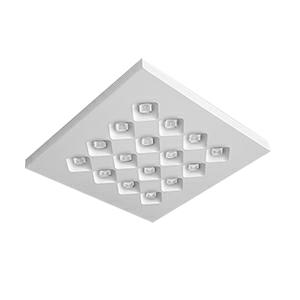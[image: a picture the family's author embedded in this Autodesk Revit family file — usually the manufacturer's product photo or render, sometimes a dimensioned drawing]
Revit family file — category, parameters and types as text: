
# Revit family: 3f_filippi_-_3f_diagon_soft_ugr_3f_filippi_-_23836_a0686_-_3f_diagon_39w-940_dali_soft_ugr_596x596___corn_plaf__04e8
name_source: partatom
category: Lighting Fixtures
units: mm (PartAtom-declared; Revit-internal decimal feet)

## family parameters
Cut with Voids When Loaded = No
Host = Face
Light Source = No
Part Type = Normal
Room Calculation Point = No
Round Connector Dimension = Use Diameter
Shared = No

## types (1)
- 3F Filippi - 3F Dìagon Soft UGR (1 x LED, 3890 lm, 40 W, 4000 K)
    Apparent Load = 40 VA
    Approval mark = CE
    CIE Flux Codes = 59 92 100 100 100
    Color Rendering = 90
    Color Temperature = 4000 K
    Control Gear = Electronic transformer
    Default Elevation = 1800 mm
    Description = ILLUMINOTECHNICAL
Luminous efficiency 100% (DLOR 100%, ULOR 0%).
Initial luminous flux of the luminaire 3890 lm.
Direct symmetric distribution.
Installation Interdistance Transv.D = 1.23 x hu - Long.D = 1.23 x hu.
Average luminance <3000 cd/m² for radial angles >65°.
Tabular UGR (CIE 117 - 4H-8H; S=0.25H; 70/50/20): RUG 18.9 - 18.9.
Beam angle: 102° - 101°.
Luminous efficacy 97 lm/W.
Lifetime (L90/B10): 30000 h. (tq+25°C)
Lifetime (L85/B10): 50000 h. (tq+25°C)
Lifetime (L80/B20): 80000 h. (tq+25°C)
Lifetime (L70/B20): 100000 h. (tq+25°C)
Sudden decreased luminous flux after 50000 hours: 0% (C0).
Photobiological safety in compliance with IEC/TR 62778: RG0 risk exempt, (IEC 62471).
In compliance with IEC/EN 62722-2-1 - IEC/EN 62717 standards.

SOURCE
Squared LED module 39W/940.
Energy efficiency class (UE 2019/2020 - UE 2019/2015): D.
CIE 13.3 Colour rendering index: CRI >90 (R9 >50%).
IES TM-30 Fidelity Index: Rf = 92 Rg = 101.
CCT nominal colour temperature 4000 K.
Colour initial tolerance (MacAdam): SDCM 3.

MECHANICAL
Housing in hot-galvanised steel, painted in white polyester.
Honeycombed diagonal screen in white anti-glare polycarbonate.
Opal methacrylate (PMMA) rhomboid lenses with differentiated, engraved and prismatic surfaces for diffused, soft lighting and excellent visual comfort.
Luminaire with limited surface temperature. - D - (EN 60598-2-24)
Dimensions: 600x600 mm, height 40 mm. Weight 6.15 kg.
IP43 protection degree for exposed part, IP20 for recessed part.
Mechanical strength to impacts IK06 (1 joule).
Glow-wire test resistance 650°C.

ELECTRICAL
Halogen Free DALI-2, PUSH-DIM, electronic wiring 230V-50/60Hz, power factor 0.97 at full load, THD <25%, constant output current, class I, 1 driver, 1 DALI addresse.
Power of the luminaire 40 W.
ENEC - CE.
SAFE FLICKER: PstLM=<1 and SVM=<0.4 (IEC TR 61547-1 and IEC TR 63158), to ensure a more comfortable and safe light.
Luminaire compliant with EN 60598-2-22 for power supply from a centralised emergency system CPSS (Central Power Supply System), not incorporated in the luminaire - high risk areas excluded. The default power and flux are 100% in AC and 15% in DC.
Ambient temperature from 0°C to +25°C.
Temperature class T6 max 85°C.
Quick connection.
Relative humidity UR: <85%.

INSTALLATION
Ceiling.
Height only 40 mm.
All accessories dedicated to this product are available on the Catalog and on our website www.3F-Filippi.com.

ACCESSORIES
A0686 - 596x596 Diagon frame for Ceiling installation.

APPLICATIONS
Environments: staterooms, with VDTs, offices.
Environments with exacting visual tasks, where diffused soft light for optimum visual comfort is required.

LIGHT MANAGEMENT
Recommended minimum setting: 10%.
The device, equipped with DALI-2 driver, can be controlled manually with 3F Easy Dim technology or automatically/manually with 3F Smart Dimming technology and/or centralised DALI systems.
DALI-2 certification guarantees interoperability with other devices with the same certification.
In electrical systems without a regulation system (manual or automatic) and DALI bus, a suitable jumper must be made on the DA-DA terminals of the appliance.

WARNING
Luminaire designed for disposal/recycling at end-of-life.
Replaceable (LED only) light source by a professional. Replaceable control gear by a professional.
    Height = 0 mm  [stored 0 ft]
    Lamp = 1 x LED
    Lamp Light Flux = 3890 lm
    Lamp Power = 40 W
    Lamp count = 1
    Length = 600 mm
    Lifetime = 50000 h
    Luminous efficacy = 97 lm/W
    Manufacturer = 3F Filippi
    ModVariant = No
    Model = 3F Filippi - 23836+A0686 - 3F Diagon 39W-940 DALI SOFT UGR 596x596 + Corn.plaf.
    Mounting Place = Ceiling
    Mounting Type = Recessed
    Number of Poles = 1
    OnlyDefault = Yes
    Power Factor = 1
    Product Name = 3F Filippi - 3F Dìagon Soft UGR
    Product group = recessed luminaire
    ProductGroupID = 4
    Protection Class = Protection class I
    Protection Degree = IP 20
    RLX_Detail_Level = 1
    RLX_Emergency_Light_Flux = 0 lm
    RLX_Emergency_Type = 0
    RLX_Emergency_Type_DB = No
    RlxData = <blob elided: 97729 chars, md5=86dff409>
    Socket = socket
    Standby Power = 0 W
    System Light Flux = 3890 lm
    System Power = 40 W
    Type Comments = Product without accessories
    Type Image = 3ffilippi_3f_diagon__a0686.jpg
    URL = http://relux.com
    VarID = ---
    Voltage = 0 V
    Weight = 0.00 kg
    Width = 600 mm

note: [stored X ft] marks values corroborated as IEEE doubles in the binary element streams (Revit-internal decimal feet)

## geometry (parser evidence)
native form markers: Blend x4, Sweep x11
no freeform markers — native parametric forms only
